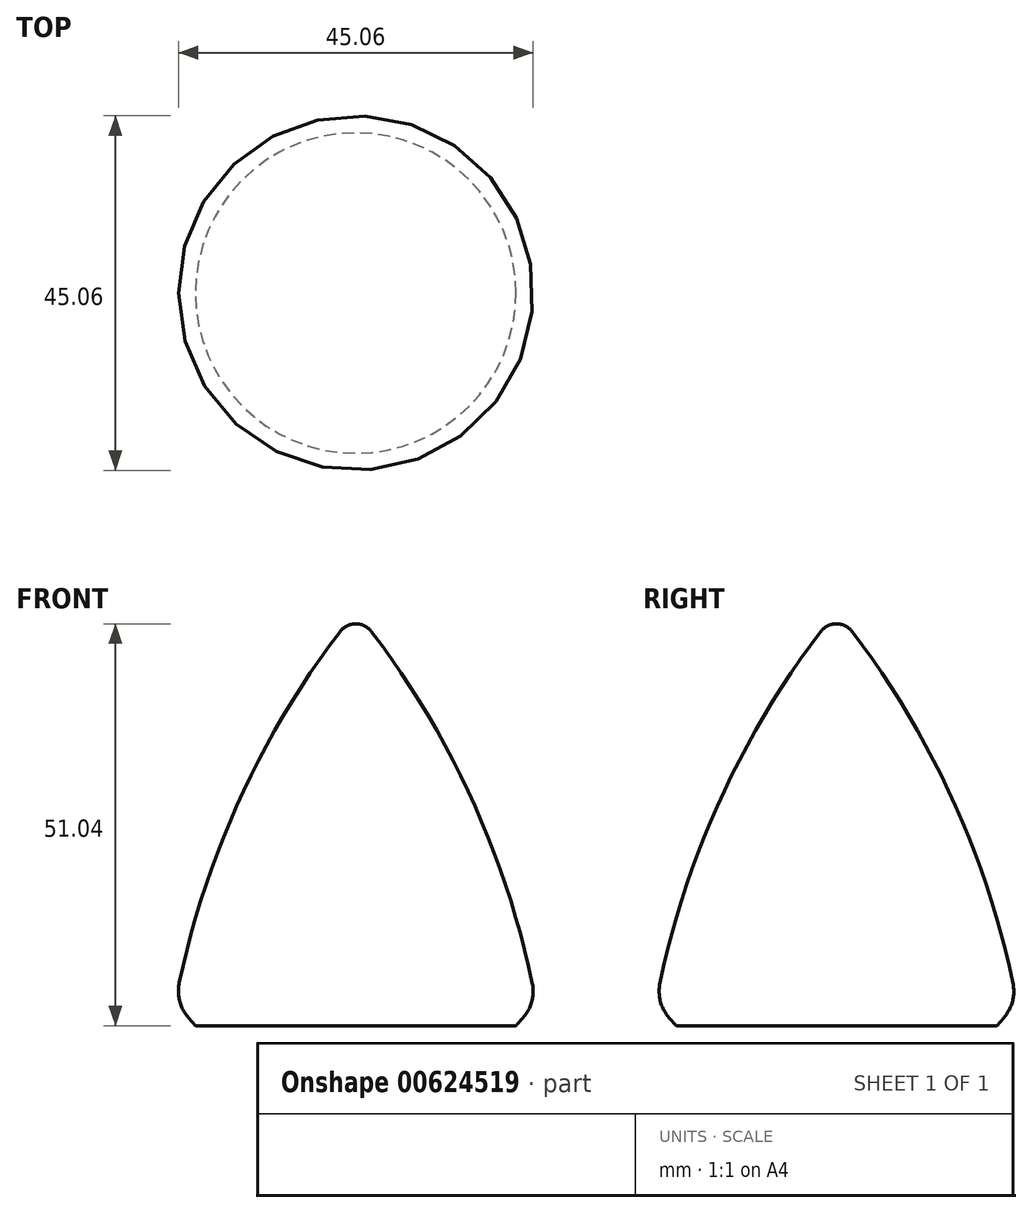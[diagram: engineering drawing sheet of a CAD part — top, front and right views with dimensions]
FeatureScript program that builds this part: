
annotation { "Feature Type Name" : "Feature", "Feature Type Description" : "" }
export const myFeature = defineFeature(function(context is Context, id is Id, definition is map)
    precondition{}
    {
        {
            var Q0;
            Q0=qCreatedBy(makeId("Front.planeOp"),FACE);
            var sketch = newSketch(context, id + "F0", { "sketchPlane" : qUnion([Q0])});
            skArc(sketch, "E0", {"start": v(-22.59, 4.6) * mm, "mid": v(-17.85, -14.59) * mm, "end": v(0, -23.05) * mm});
            skLineSegment(sketch, "E1", {"start": v(0, 52.62) * mm, "end": v(0, 51.04) * mm});
            skArc(sketch, "E2", {"start": v(-2.02, 50.04) * mm, "mid": v(-14.87, 28.47) * mm, "end": v(-22.59, 4.6) * mm});
            skPoint(sketch, "E3.visualSharp", {"position": v(0, 52.62) * mm});
            skLineSegment(sketch, "E4", {"start": v(0, 51.04) * mm, "end": v(0, -23.05) * mm});
            skArc(sketch, "E5", {"start": v(0, 51.04) * mm, "mid": v(-1.13, 50.78) * mm, "end": v(-2.02, 50.04) * mm});
            skSolve(sketch);
        }
        {
            var Q0;
            Q0=makeQuery(id+"F0.imprint","IMPRINT",FACE,{"disambiguationData":[TD([[makeQuery(id+"F0.imprint","IMPRINT",EDGE,{"derivedFrom":sQuery(id+"F0.wireOp",EDGE,"E0")}),1.0]])]});
            var Q1;
            Q1=sQuery(id+"F0.wireOp",EDGE,"E4");
            revolve(context, id + "F1", {"entities" : qUnion([Q0]), "axis" : qUnion([Q1]), "revolveType" : RevolveType.FULL});
        }
        {
            var Q0;
            Q0=qCreatedBy(makeId("Top.planeOp"),FACE);
            var sketch = newSketch(context, id + "F2", { "sketchPlane" : qUnion([Q0])});
            skCircle(sketch, "E6", {"center": v(0, 0) * mm, "radius": 36.14 * mm});
            skSolve(sketch);
        }
        {
            var Q0;
            Q0=makeQuery(id+"F2.imprint","IMPRINT",FACE,{"disambiguationData":[TD([[makeQuery(id+"F2.imprint","IMPRINT",EDGE,{"derivedFrom":sQuery(id+"F2.wireOp",EDGE,"E6")}),1.0]])]});
            extrude(context, id + "F3", {"entities" : qUnion([Q0]), "operationType" : NewBodyOperationType.REMOVE, "oppositeDirection" : true, "depth" : 25.4 * mm, "offsetDistance" : 25.4 * mm});
        }
        {
            var Q0;
            Q0=makeQuery(id+"F3.boolean.opBoolean","INTERSECT",EDGE,{"derivedFrom":[makeQuery(id+"F1.opRevolve","SWEPT_FACE",FACE,{"disambiguationData":[OSD([sQuery(id+"F0.wireOp",EDGE,"E0")])]}),makeQuery(id+"F3.opExtrude","CAP_FACE",FACE,{"disambiguationData":[OSD([sQuery(id+"F2.wireOp",EDGE,"E6")])],"isStart":true})]});
            chamfer(context, id + "F4", {"entities" : qUnion([Q0]), "width" : 2.54 * mm, "tangentPropagation" : true});
        }
        {
            var Q0;
            {var subQ0=makeQuery(id+"F1.opRevolve","SWEPT_FACE",FACE,{"disambiguationData":[OSD([sQuery(id+"F0.wireOp",EDGE,"E0")])]});Q0=makeQuery(id+"F4.opChamfer","BLEND_EDGE",EDGE,{"blendedFrom":[makeQuery(id+"F3.boolean.opBoolean","INTERSECT",EDGE,{"derivedFrom":[subQ0,makeQuery(id+"F3.opExtrude","CAP_FACE",FACE,{"disambiguationData":[OSD([sQuery(id+"F2.wireOp",EDGE,"E6")])],"isStart":true})]}),subQ0],"blendedInto":[subQ0]});}
            fillet(context, id + "F5", {"entities" : qUnion([Q0]), "radius" : 5.08 * mm, "tangentPropagation" : true, "allowEdgeOverflow" : false});
        }
    });
